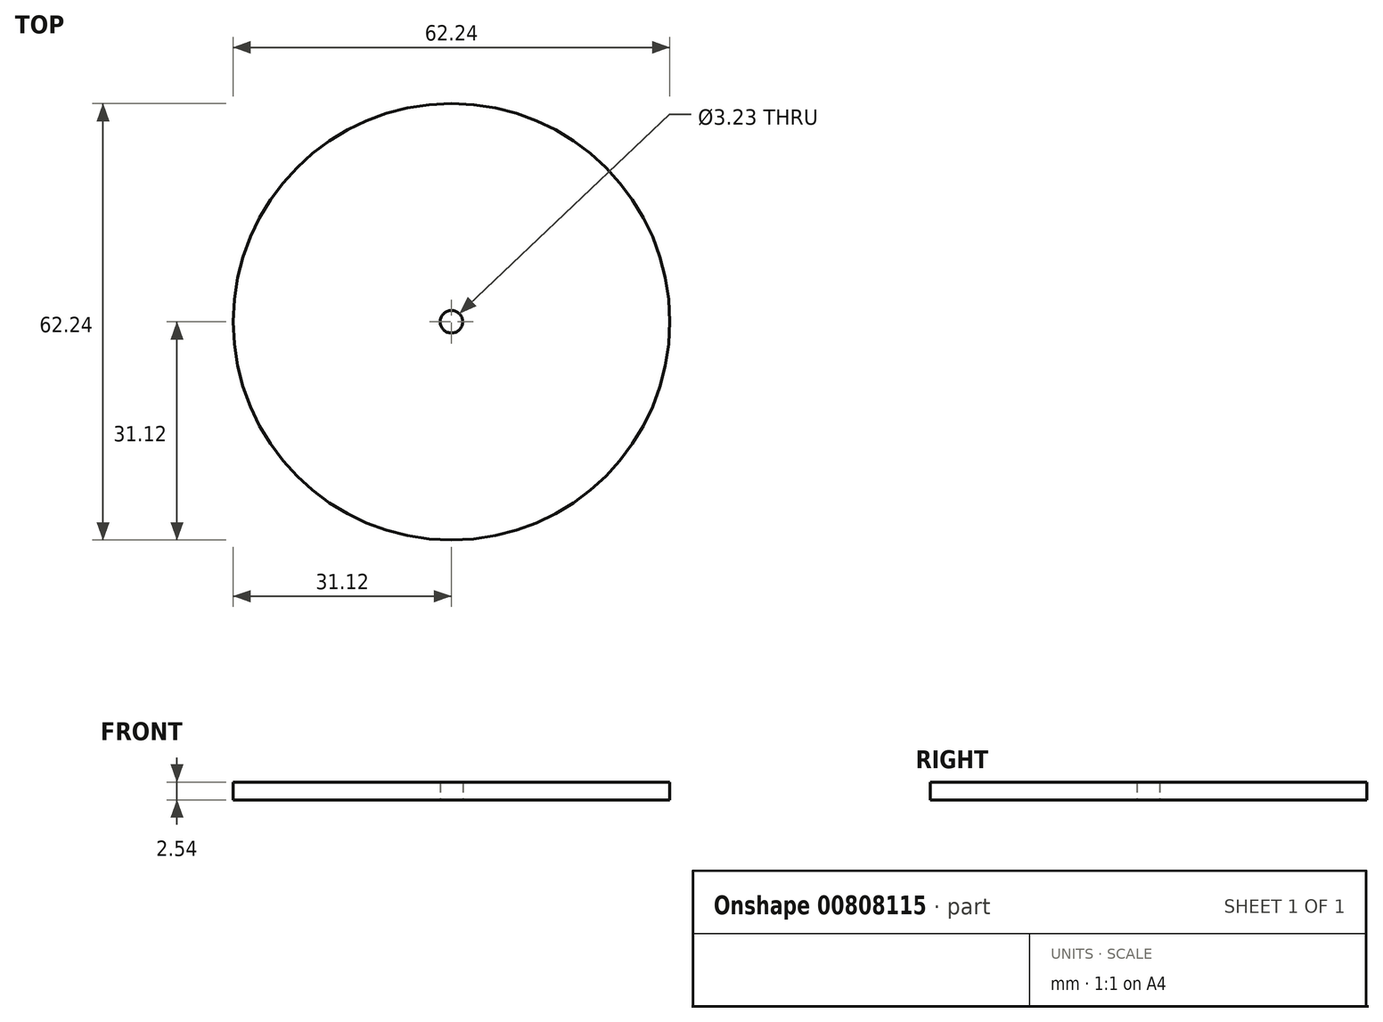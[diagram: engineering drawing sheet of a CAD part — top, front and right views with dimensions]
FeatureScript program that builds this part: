
annotation { "Feature Type Name" : "Feature", "Feature Type Description" : "" }
export const myFeature = defineFeature(function(context is Context, id is Id, definition is map)
    precondition{}
    {
        {
            var Q0;
            Q0=qCreatedBy(makeId("Top.planeOp"),FACE);
            var sketch = newSketch(context, id + "F0", { "sketchPlane" : qUnion([Q0])});
            skCircle(sketch, "E0", {"center": v(0, 0) * mm, "radius": 31.12 * mm});
            skCircle(sketch, "E1", {"center": v(0, 0) * mm, "radius": 1.61 * mm});
            skSolve(sketch);
        }
        {
            var Q0;
            Q0=qSketchRegion(id+"F0",true);
            extrude(context, id + "F1", {"entities" : qUnion([Q0]), "depth" : 2.54 * mm, "offsetDistance" : 25.4 * mm});
        }
    });
